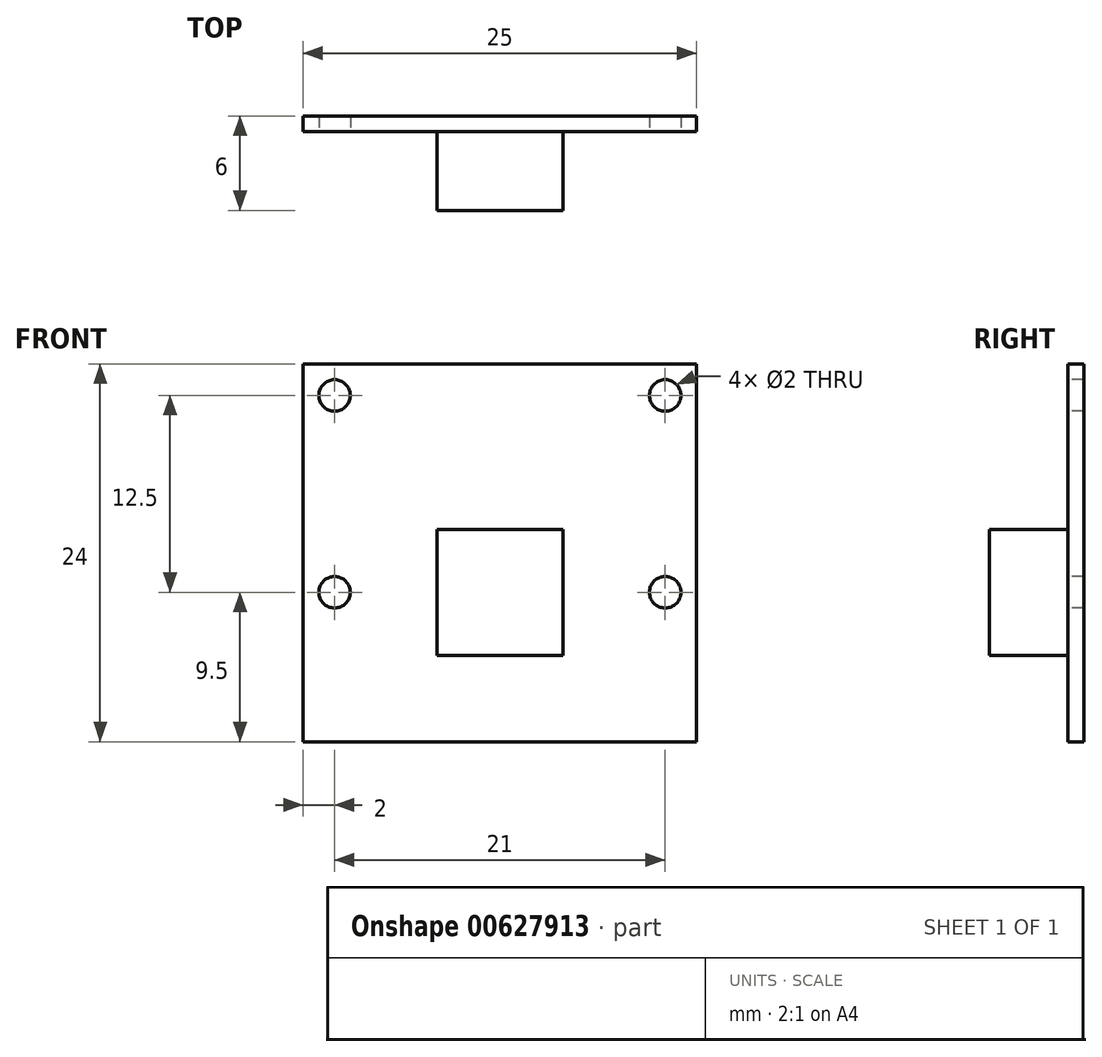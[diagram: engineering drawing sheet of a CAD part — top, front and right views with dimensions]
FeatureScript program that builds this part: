
annotation { "Feature Type Name" : "Feature", "Feature Type Description" : "" }
export const myFeature = defineFeature(function(context is Context, id is Id, definition is map)
    precondition{}
    {
        {
            var Q0;
            Q0=qCreatedBy(makeId("Front.planeOp"),FACE);
            var sketch = newSketch(context, id + "F0", { "sketchPlane" : qUnion([Q0])});
            skLineSegment(sketch, "E0.bottom", {"start": v(-12.5, 12) * mm, "end": v(12.5, 12) * mm});
            skLineSegment(sketch, "E0.top", {"start": v(-12.5, -12) * mm, "end": v(12.5, -12) * mm});
            skLineSegment(sketch, "E0.left", {"start": v(-12.5, 12) * mm, "end": v(-12.5, -12) * mm});
            skLineSegment(sketch, "E0.right", {"start": v(12.5, 12) * mm, "end": v(12.5, -12) * mm});
            skPoint(sketch, "E0.middle", {"position": v(0, 0) * mm});
            skSolve(sketch);
        }
        {
            var Q0;
            Q0 = qSketchRegion(id + "F0", true);
            extrude(context, id + "F1", {"entities" : qUnion([Q0]), "flatOperationType" : FlatOperationType.REMOVE, "depth" : 1 * mm, "offsetDistance" : 25.4 * mm, "domain" : OperationDomain.MODEL});
        }
        {
            var Q0;
            Q0=makeQuery(id+"F1.opExtrude","CAP_FACE",FACE,{"disambiguationData":[OSD([sQuery(id+"F0.wireOp",EDGE,"E0.bottom"),sQuery(id+"F0.wireOp",EDGE,"E0.top"),sQuery(id+"F0.wireOp",EDGE,"E0.left"),sQuery(id+"F0.wireOp",EDGE,"E0.right")])],"isStart":false});
            var sketch = newSketch(context, id + "F2", { "sketchPlane" : qUnion([Q0])});
            skLineSegment(sketch, "E1.bottom", {"start": v(4, -6.5) * mm, "end": v(-4, -6.5) * mm});
            skLineSegment(sketch, "E1.top", {"start": v(4, 1.5) * mm, "end": v(-4, 1.5) * mm});
            skLineSegment(sketch, "E1.left", {"start": v(4, -6.5) * mm, "end": v(4, 1.5) * mm});
            skLineSegment(sketch, "E1.right", {"start": v(-4, -6.5) * mm, "end": v(-4, 1.5) * mm});
            skPoint(sketch, "E1.middle", {"position": v(0, -2.5) * mm});
            skSolve(sketch);
        }
        {
            var Q0;
            Q0 = qSketchRegion(id + "F2", true);
            extrude(context, id + "F3", {"entities" : qUnion([Q0]), "operationType" : NewBodyOperationType.ADD, "depth" : 5 * mm, "offsetDistance" : 25.4 * mm});
        }
        {
            var Q0;
            Q0=makeQuery(id+"F1.opExtrude","CAP_FACE",FACE,{"disambiguationData":[OSD([sQuery(id+"F0.wireOp",EDGE,"E0.bottom"),sQuery(id+"F0.wireOp",EDGE,"E0.top"),sQuery(id+"F0.wireOp",EDGE,"E0.left"),sQuery(id+"F0.wireOp",EDGE,"E0.right")])],"isStart":false});
            var sketch = newSketch(context, id + "F4", { "sketchPlane" : qUnion([Q0])});
            skCircle(sketch, "E2", {"center": v(-10.5, 10) * mm, "radius": 1 * mm});
            skCircle(sketch, "E3", {"center": v(-10.5, -2.5) * mm, "radius": 1 * mm});
            skCircle(sketch, "E4", {"center": v(10.5, -2.5) * mm, "radius": 1 * mm});
            skCircle(sketch, "E5", {"center": v(10.5, 10) * mm, "radius": 1 * mm});
            skSolve(sketch);
        }
        {
            var Q0;
            Q0=makeQuery(id+"F4.imprint","IMPRINT",FACE,{"disambiguationData":[TD([[makeQuery(id+"F4.imprint","IMPRINT",EDGE,{"derivedFrom":sQuery(id+"F4.wireOp",EDGE,"E5")}),1.0]])]});
            var Q1;
            Q1=makeQuery(id+"F4.imprint","IMPRINT",FACE,{"disambiguationData":[TD([[makeQuery(id+"F4.imprint","IMPRINT",EDGE,{"derivedFrom":sQuery(id+"F4.wireOp",EDGE,"E2")}),1.0]])]});
            var Q2;
            Q2=makeQuery(id+"F4.imprint","IMPRINT",FACE,{"disambiguationData":[TD([[makeQuery(id+"F4.imprint","IMPRINT",EDGE,{"derivedFrom":sQuery(id+"F4.wireOp",EDGE,"E3")}),1.0]])]});
            var Q3;
            Q3=makeQuery(id+"F4.imprint","IMPRINT",FACE,{"disambiguationData":[TD([[makeQuery(id+"F4.imprint","IMPRINT",EDGE,{"derivedFrom":sQuery(id+"F4.wireOp",EDGE,"E4")}),1.0]])]});
            extrude(context, id + "F5", {"entities" : qUnion([Q0, Q1, Q2, Q3]), "operationType" : NewBodyOperationType.REMOVE, "endBound" : BoundingType.THROUGH_ALL, "oppositeDirection" : true, "depth" : 25.4 * mm, "offsetDistance" : 25.4 * mm});
        }
    });
